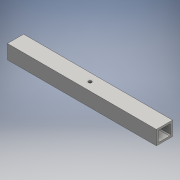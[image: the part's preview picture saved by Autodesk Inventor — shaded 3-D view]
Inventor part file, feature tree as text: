
AUTODESK INVENTOR PART (.ipt)
format: ipt  version: 2016 (Build 200138000, 138)  size: 116,736 bytes
history: native  units: mm
features: extrude x3, sketch x3, fillet x1
ambient origin geometry x8: Origin, YZ Plane, XZ Plane, XY Plane, X Axis, Y Axis, Z Axis, Center Point
bodies: Body1 (feature_tree)
feature tree (7):
  extrude  "Extrusion2"  Depth=15.0mm
  extrude  "Extrusion3"  Depth=11.0mm
  extrude  "Extrusion4"  TaperAngle=0.0deg  [1 undecoded]
  fillet  "Fillet1"  Radius=3.5mm
  sketch  "Sketch2"  dims[d4=17.0mm d5=15.0mm]
  sketch  "Sketch3"  dims[d6=157.0mm d7=0.0mm d9=11.0mm]
  sketch  "Sketch5"  dims[d10=13.0mm d11=0.0mm d12=0.0mm d13=3.5mm d14=250.0mm d15=0.0mm d16=1.0mm]
note: 1 required parameter value undecoded (feature->parameter linkage not recoverable at this tier; creation-order binding heuristic only, values carry confidence <= 0.55)
